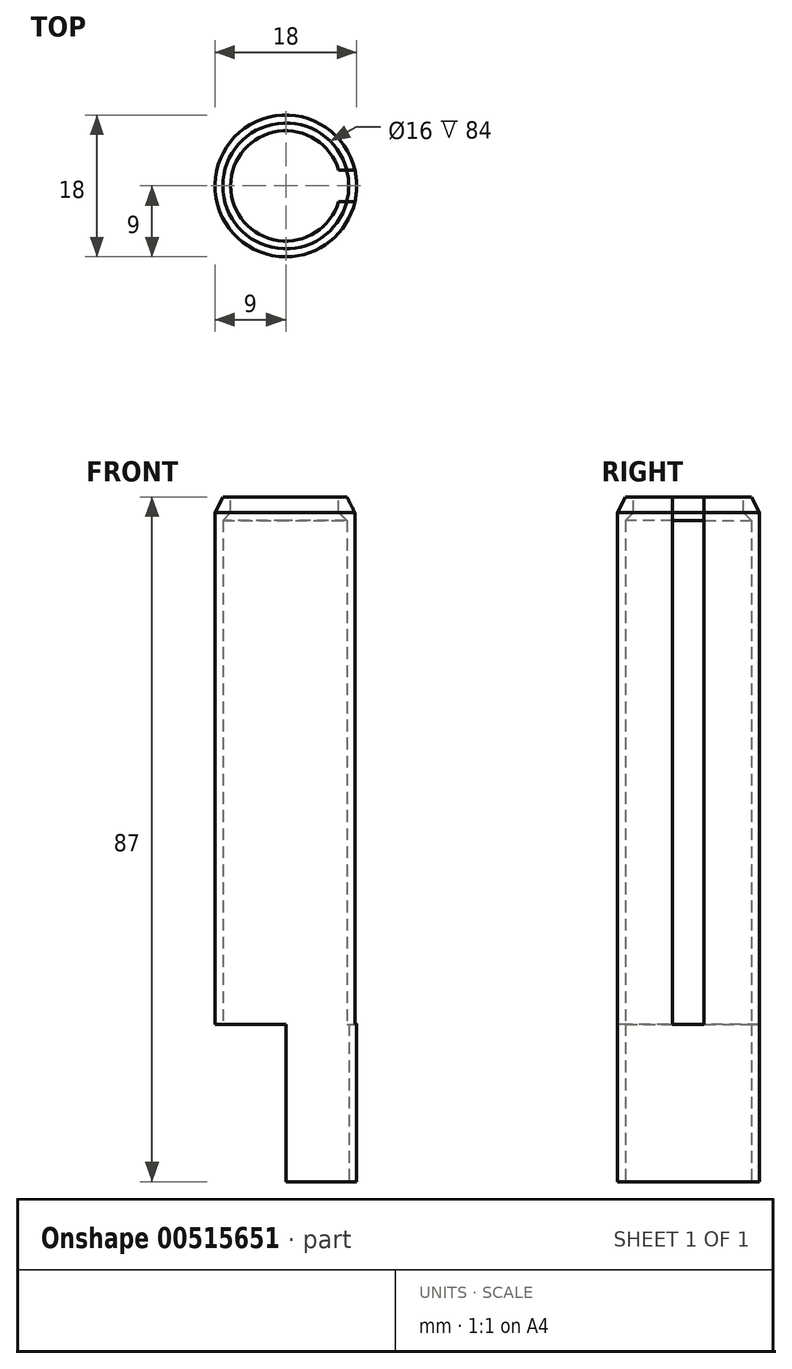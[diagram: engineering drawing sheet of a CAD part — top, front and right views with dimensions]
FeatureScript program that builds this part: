
annotation { "Feature Type Name" : "Feature", "Feature Type Description" : "" }
export const myFeature = defineFeature(function(context is Context, id is Id, definition is map)
    precondition{}
    {
        {
            var Q0;
            Q0=qCreatedBy(makeId("Top.planeOp"),FACE);
            var sketch = newSketch(context, id + "F0", { "sketchPlane" : qUnion([Q0])});
            skCircle(sketch, "E0", {"center": v(0, 0) * mm, "radius": 9 * mm});
            skSolve(sketch);
        }
        {
            var Q0;
            Q0 = qSketchRegion(id + "F0", true);
            extrude(context, id + "F1", {"entities" : qUnion([Q0]), "depth" : 40 * mm, "offsetDistance" : 25 * mm});
        }
        {
            var Q0;
            Q0=qCreatedBy(makeId("Top.planeOp"),FACE);
            cPlane(context, id + "F2", {"entities" : qUnion([Q0]), "cplaneType" : CPlaneType.OFFSET, "offset" : 42 * mm, "width" : 150 * mm, "height" : 150 * mm});
        }
        {
            var Q0;
            Q0=makeQuery(id+"F1.opExtrude","CAP_FACE",FACE,{"disambiguationData":[OSD([sQuery(id+"F0.wireOp",EDGE,"E0")])],"isStart":false});
            var sketch = newSketch(context, id + "F3", { "sketchPlane" : qUnion([Q0])});
            skSolve(sketch);
        }
        {
            var Q0;
            Q0=qCreatedBy(id+"F2.planeOp",FACE);
            var sketch = newSketch(context, id + "F4", { "sketchPlane" : qUnion([Q0])});
            skCircle(sketch, "E1", {"center": v(0, 0) * mm, "radius": 8 * mm});
            skSolve(sketch);
        }
        {
            var Q0;
            Q0=makeQuery(id+"F3.imprint","IMPRINT",FACE,{"disambiguationData":[TD([[makeQuery(id+"F3.imprint","IMPRINT",EDGE,{"derivedFrom":makeQuery(id+"F1.opExtrude","CAP_EDGE",EDGE,{"disambiguationData":[OSD([sQuery(id+"F0.wireOp",EDGE,"E0")])],"isStart":false})}),1.0]])]});
            var Q1;
            Q1=makeQuery(id+"F4.imprint","IMPRINT",FACE,{"disambiguationData":[TD([[makeQuery(id+"F4.imprint","IMPRINT",EDGE,{"derivedFrom":sQuery(id+"F4.wireOp",EDGE,"E1")}),1.0]])]});
            loft(context, id + "F5", {"operationType" : NewBodyOperationType.ADD, "sheetProfilesArray" : [{ "sheetProfileEntities" : qUnion([Q0]) }, { "sheetProfileEntities" : qUnion([Q1]) }]});
        }
        {
            var Q0;
            Q0=makeQuery(id+"F1.opExtrude","CAP_FACE",FACE,{"disambiguationData":[OSD([sQuery(id+"F0.wireOp",EDGE,"E0")])],"isStart":true});
            var sketch = newSketch(context, id + "F6", { "sketchPlane" : qUnion([Q0])});
            skCircle(sketch, "E2", {"center": v(0, 0) * mm, "radius": 8 * mm});
            skSolve(sketch);
        }
        {
            var Q0;
            Q0=makeQuery(id+"F5.opLoft","CAP_FACE",FACE,{"disambiguationData":[OSD([makeQuery(id+"F4.imprint","IMPRINT",FACE,{"disambiguationData":[TD([[makeQuery(id+"F4.imprint","IMPRINT",EDGE,{"derivedFrom":sQuery(id+"F4.wireOp",EDGE,"E1")}),1.0]])]})])],"isStart":true});
            var sketch = newSketch(context, id + "F7", { "sketchPlane" : qUnion([Q0])});
            skCircle(sketch, "E3", {"center": v(0, 0) * mm, "radius": 7 * mm});
            skSolve(sketch);
        }
        {
            var Q0;
            Q0 = qSketchRegion(id + "F6", true);
            extrude(context, id + "F8", {"entities" : qUnion([Q0]), "operationType" : NewBodyOperationType.REMOVE, "oppositeDirection" : true, "depth" : 39 * mm, "offsetDistance" : 25 * mm});
        }
        {
            var Q0;
            Q0=makeQuery(id+"F1.opExtrude","CAP_FACE",FACE,{"disambiguationData":[OSD([sQuery(id+"F0.wireOp",EDGE,"E0")])],"isStart":true});
            var sketch = newSketch(context, id + "F9", { "sketchPlane" : qUnion([Q0])});
            skCircle(sketch, "E4", {"center": v(0, 0) * mm, "radius": 9 * mm});
            skCircle(sketch, "E5", {"center": v(0, 0) * mm, "radius": 8 * mm});
            skSolve(sketch);
        }
        {
            var Q0;
            Q0 = qSketchRegion(id + "F9", true);
            extrude(context, id + "F10", {"entities" : qUnion([Q0]), "operationType" : NewBodyOperationType.ADD, "depth" : 45 * mm, "offsetDistance" : 25 * mm});
        }
        {
            var Q0;
            Q0=makeQuery(id+"F10.opExtrude","CAP_FACE",FACE,{"disambiguationData":[OSD([sQuery(id+"F9.wireOp",EDGE,"E4"),sQuery(id+"F9.wireOp",EDGE,"E5")])],"isStart":false});
            var sketch = newSketch(context, id + "F11", { "sketchPlane" : qUnion([Q0])});
            skCircle(sketch, "E6", {"center": v(0, 0) * mm, "radius": 9 * mm});
            skLineSegment(sketch, "E7", {"start": v(0, 0) * mm, "end": v(0, -9) * mm});
            skLineSegment(sketch, "E8", {"start": v(0, -9) * mm, "end": v(0, 9) * mm});
            skSolve(sketch);
        }
        {
            var Q0;
            {var subQ0=sQuery(id+"F11.wireOp",EDGE,"E8");var subQ1=sQuery(id+"F11.wireOp",EDGE,"E6");var subQ2=makeQuery(id+"F11.imprint","INTERSECT",VERTEX,{"disambiguationData":[OD(0.0)],"derivedFrom":[subQ1,subQ0]});Q0=makeQuery(id+"F11.imprint","IMPRINT",FACE,{"disambiguationData":[TD([[makeQuery(id+"F11.imprint","IMPRINT",EDGE,{"disambiguationData":[TD([[subQ2,1.0]])],"derivedFrom":subQ1}),-1.0]])]});}
            extrude(context, id + "F12", {"entities" : qUnion([Q0]), "operationType" : NewBodyOperationType.REMOVE, "oppositeDirection" : true, "depth" : 20 * mm, "offsetDistance" : 25 * mm});
        }
        {
            var Q0;
            Q0=makeQuery(id+"F12.boolean.opBoolean","COPY",FACE,{"derivedFrom":makeQuery(id+"F12.opExtrude","CAP_FACE",FACE,{"disambiguationData":[OSD([sQuery(id+"F9.wireOp",EDGE,"E5"),sQuery(id+"F11.wireOp",EDGE,"E6"),sQuery(id+"F11.wireOp",EDGE,"E8")])],"isStart":false})});
            var sketch = newSketch(context, id + "F13", { "sketchPlane" : qUnion([Q0])});
            skLineSegment(sketch, "E9.bottom", {"start": v(6, -2) * mm, "end": v(10, -2) * mm});
            skLineSegment(sketch, "E9.top", {"start": v(6, 2) * mm, "end": v(10, 2) * mm});
            skLineSegment(sketch, "E9.left", {"start": v(6, -2) * mm, "end": v(6, 2) * mm});
            skLineSegment(sketch, "E9.right", {"start": v(10, -2) * mm, "end": v(10, 2) * mm});
            skPoint(sketch, "E9.middle", {"position": v(8, 0) * mm});
            skSolve(sketch);
        }
        {
            var Q0;
            Q0 = qSketchRegion(id + "F13", true);
            extrude(context, id + "F14", {"entities" : qUnion([Q0]), "operationType" : NewBodyOperationType.REMOVE, "oppositeDirection" : true, "depth" : 100 * mm, "offsetDistance" : 25 * mm});
        }
        {
            var Q0;
            Q0=makeQuery(id+"F7.imprint","IMPRINT",FACE,{"disambiguationData":[TD([[makeQuery(id+"F7.imprint","IMPRINT",EDGE,{"derivedFrom":sQuery(id+"F7.wireOp",EDGE,"E3")}),1.0]])]});
            extrude(context, id + "F15", {"entities" : qUnion([Q0]), "operationType" : NewBodyOperationType.REMOVE, "oppositeDirection" : true, "depth" : 25 * mm, "offsetDistance" : 25 * mm});
        }
        {
            var Q0;
            Q0=makeQuery(id+"F15.boolean.opBoolean","INTERSECT",EDGE,{"derivedFrom":[makeQuery(id+"F8.boolean.opBoolean","COPY",FACE,{"derivedFrom":makeQuery(id+"F8.opExtrude","CAP_FACE",FACE,{"disambiguationData":[OSD([sQuery(id+"F6.wireOp",EDGE,"E2")])],"isStart":false})}),makeQuery(id+"F15.opExtrude","SWEPT_FACE",FACE,{"disambiguationData":[OSD([sQuery(id+"F7.wireOp",EDGE,"E3")])]})]});
            chamfer(context, id + "F16", {"entities" : qUnion([Q0]), "chamferType" : ChamferType.TWO_OFFSETS, "width1" : 1 * mm, "oppositeDirection" : false, "width2" : 1 * mm, "tangentPropagation" : true});
        }
    });
